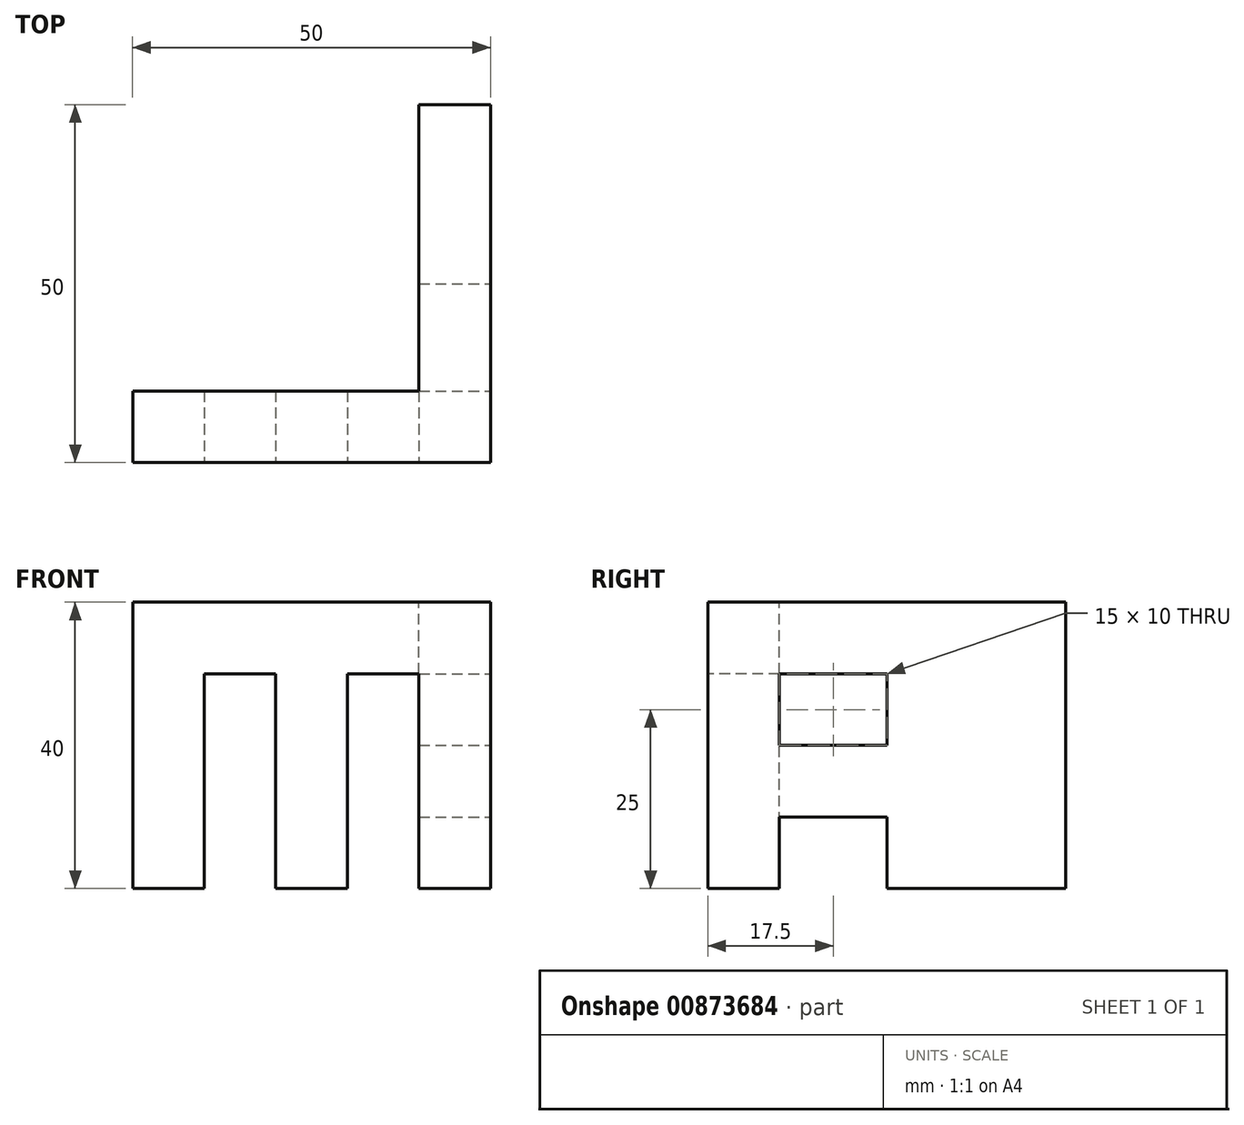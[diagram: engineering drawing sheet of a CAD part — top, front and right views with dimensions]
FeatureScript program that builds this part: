
annotation { "Feature Type Name" : "Feature", "Feature Type Description" : "" }
export const myFeature = defineFeature(function(context is Context, id is Id, definition is map)
    precondition{}
    {
        {
            var Q0;
            Q0=qCreatedBy(makeId("Front.planeOp"),FACE);
            var sketch = newSketch(context, id + "F0", { "sketchPlane" : qUnion([Q0])});
            skLineSegment(sketch, "E0.bottom", {"start": v(-85.35, 0) * mm, "end": v(-35.35, 0) * mm});
            skLineSegment(sketch, "E0.top", {"start": v(-85.35, 40) * mm, "end": v(-35.35, 40) * mm});
            skLineSegment(sketch, "E0.left", {"start": v(-85.35, 0) * mm, "end": v(-85.35, 40) * mm});
            skLineSegment(sketch, "E0.right", {"start": v(-35.35, 0) * mm, "end": v(-35.35, 40) * mm});
            skSolve(sketch);
        }
        {
            var Q0;
            Q0=makeQuery(id+"F0.imprint","IMPRINT",FACE,{"disambiguationData":[TD([[makeQuery(id+"F0.imprint","IMPRINT",EDGE,{"derivedFrom":sQuery(id+"F0.wireOp",EDGE,"E0.bottom")}),1.0]])]});
            extrude(context, id + "F1", {"entities" : qUnion([Q0]), "depth" : 50 * mm, "offsetDistance" : 25 * mm});
        }
        {
            var Q0;
            Q0=makeQuery(id+"F1.opExtrude","SWEPT_FACE",FACE,{"disambiguationData":[OSD([sQuery(id+"F0.wireOp",EDGE,"E0.top")])]});
            var sketch = newSketch(context, id + "F2", { "sketchPlane" : qUnion([Q0])});
            skLineSegment(sketch, "E1.bottom", {"start": v(-85.35, 0) * mm, "end": v(-45.35, 0) * mm});
            skLineSegment(sketch, "E1.top", {"start": v(-85.35, -40) * mm, "end": v(-45.35, -40) * mm});
            skLineSegment(sketch, "E1.left", {"start": v(-85.35, 0) * mm, "end": v(-85.35, -40) * mm});
            skLineSegment(sketch, "E1.right", {"start": v(-45.35, 0) * mm, "end": v(-45.35, -40) * mm});
            skSolve(sketch);
        }
        {
            var Q0;
            Q0 = qSketchRegion(id + "F2", true);
            extrude(context, id + "F3", {"entities" : qUnion([Q0]), "operationType" : NewBodyOperationType.REMOVE, "oppositeDirection" : true, "depth" : 50 * mm, "offsetDistance" : 25 * mm});
        }
        {
            var Q0;
            Q0=makeQuery(id+"F1.opExtrude","CAP_FACE",FACE,{"disambiguationData":[OSD([sQuery(id+"F0.wireOp",EDGE,"E0.bottom"),sQuery(id+"F0.wireOp",EDGE,"E0.top"),sQuery(id+"F0.wireOp",EDGE,"E0.left"),sQuery(id+"F0.wireOp",EDGE,"E0.right")])],"isStart":false});
            var sketch = newSketch(context, id + "F4", { "sketchPlane" : qUnion([Q0])});
            skLineSegment(sketch, "E2.bottom", {"start": v(-75.35, 0) * mm, "end": v(-65.35, 0) * mm});
            skLineSegment(sketch, "E2.top", {"start": v(-75.35, 30) * mm, "end": v(-65.35, 30) * mm});
            skLineSegment(sketch, "E2.left", {"start": v(-75.35, 0) * mm, "end": v(-75.35, 30) * mm});
            skLineSegment(sketch, "E2.right", {"start": v(-65.35, 0) * mm, "end": v(-65.35, 30) * mm});
            skLineSegment(sketch, "E3.bottom", {"start": v(-55.35, 0) * mm, "end": v(-45.35, 0) * mm});
            skLineSegment(sketch, "E3.top", {"start": v(-55.35, 30) * mm, "end": v(-45.35, 30) * mm});
            skLineSegment(sketch, "E3.left", {"start": v(-55.35, 0) * mm, "end": v(-55.35, 30) * mm});
            skLineSegment(sketch, "E3.right", {"start": v(-45.35, 0) * mm, "end": v(-45.35, 30) * mm});
            skLineSegment(sketch, "E4.bottom", {"start": v(-75.35, 40) * mm, "end": v(-65.35, 40) * mm});
            skSolve(sketch);
        }
        {
            var Q0;
            Q0 = qSketchRegion(id + "F4", true);
            extrude(context, id + "F5", {"entities" : qUnion([Q0]), "operationType" : NewBodyOperationType.REMOVE, "oppositeDirection" : true, "depth" : 10 * mm, "offsetDistance" : 25 * mm});
        }
        {
            var Q0;
            Q0=makeQuery(id+"F1.opExtrude","SWEPT_FACE",FACE,{"disambiguationData":[OSD([sQuery(id+"F0.wireOp",EDGE,"E0.right")])]});
            var sketch = newSketch(context, id + "F6", { "sketchPlane" : qUnion([Q0])});
            skLineSegment(sketch, "E5.bottom", {"start": v(-40, 30) * mm, "end": v(-25, 30) * mm});
            skLineSegment(sketch, "E5.top", {"start": v(-40, 20) * mm, "end": v(-25, 20) * mm});
            skLineSegment(sketch, "E5.left", {"start": v(-40, 30) * mm, "end": v(-40, 20) * mm});
            skLineSegment(sketch, "E5.right", {"start": v(-25, 30) * mm, "end": v(-25, 20) * mm});
            skLineSegment(sketch, "E6.bottom", {"start": v(-40, 10) * mm, "end": v(-25, 10) * mm});
            skLineSegment(sketch, "E6.top", {"start": v(-40, 0) * mm, "end": v(-25, 0) * mm});
            skLineSegment(sketch, "E6.left", {"start": v(-40, 10) * mm, "end": v(-40, 0) * mm});
            skLineSegment(sketch, "E6.right", {"start": v(-25, 10) * mm, "end": v(-25, 0) * mm});
            skSolve(sketch);
        }
        {
            var Q0;
            Q0 = qSketchRegion(id + "F6", true);
            extrude(context, id + "F7", {"entities" : qUnion([Q0]), "operationType" : NewBodyOperationType.REMOVE, "oppositeDirection" : true, "depth" : 10 * mm, "offsetDistance" : 25 * mm});
        }
    });
